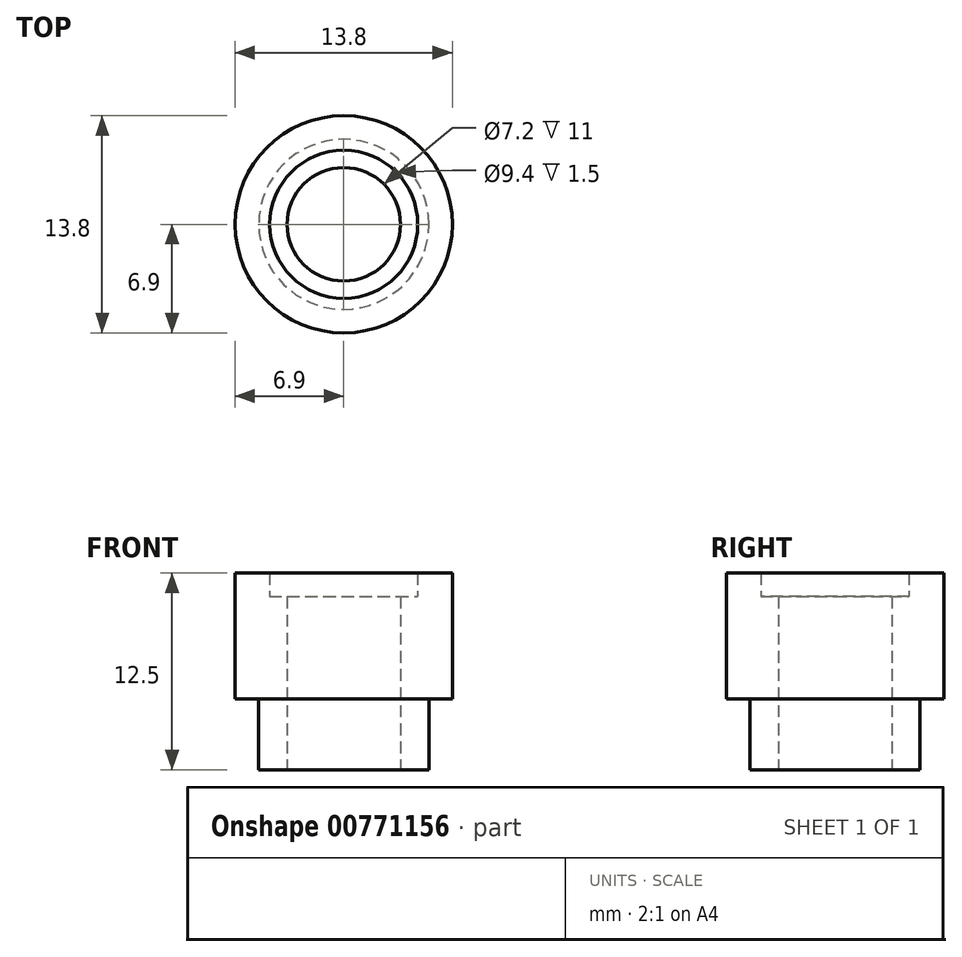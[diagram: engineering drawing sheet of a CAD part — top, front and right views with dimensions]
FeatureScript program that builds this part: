
annotation { "Feature Type Name" : "Feature", "Feature Type Description" : "" }
export const myFeature = defineFeature(function(context is Context, id is Id, definition is map)
    precondition{}
    {
        {
            var Q0;
            Q0=qCreatedBy(makeId("Front.planeOp"),FACE);
            var sketch = newSketch(context, id + "F0", { "sketchPlane" : qUnion([Q0])});
            skLineSegment(sketch, "E0", {"start": v(0, 0) * mm, "end": v(0, 15.61) * mm, "construction": true});
            skLineSegment(sketch, "E1", {"start": v(-3.6, 0) * mm, "end": v(-3.6, 11) * mm});
            skLineSegment(sketch, "E2", {"start": v(-3.6, 11) * mm, "end": v(-4.7, 11) * mm});
            skLineSegment(sketch, "E3", {"start": v(-4.7, 11) * mm, "end": v(-4.7, 12.5) * mm});
            skLineSegment(sketch, "E4", {"start": v(-4.7, 12.5) * mm, "end": v(-6.9, 12.5) * mm});
            skLineSegment(sketch, "E5", {"start": v(-6.9, 12.5) * mm, "end": v(-6.9, 4.5) * mm});
            skLineSegment(sketch, "E6", {"start": v(-6.9, 4.5) * mm, "end": v(-5.4, 4.5) * mm});
            skLineSegment(sketch, "E7", {"start": v(-5.4, 4.5) * mm, "end": v(-5.4, 0) * mm});
            skLineSegment(sketch, "E8", {"start": v(-5.4, 0) * mm, "end": v(-3.6, 0) * mm});
            skSolve(sketch);
        }
        {
            var Q0;
            Q0=makeQuery(id+"F0.imprint","IMPRINT",FACE,{"disambiguationData":[TD([[makeQuery(id+"F0.imprint","IMPRINT",EDGE,{"derivedFrom":sQuery(id+"F0.wireOp",EDGE,"E1")}),1.0]])]});
            var Q1;
            Q1=sQuery(id+"F0.wireOp",EDGE,"E0");
            revolve(context, id + "F1", {"surfaceOperationType" : NewSurfaceOperationType.NEW, "entities" : qUnion([Q0]), "axis" : qUnion([Q1]), "revolveType" : RevolveType.FULL});
        }
    });
